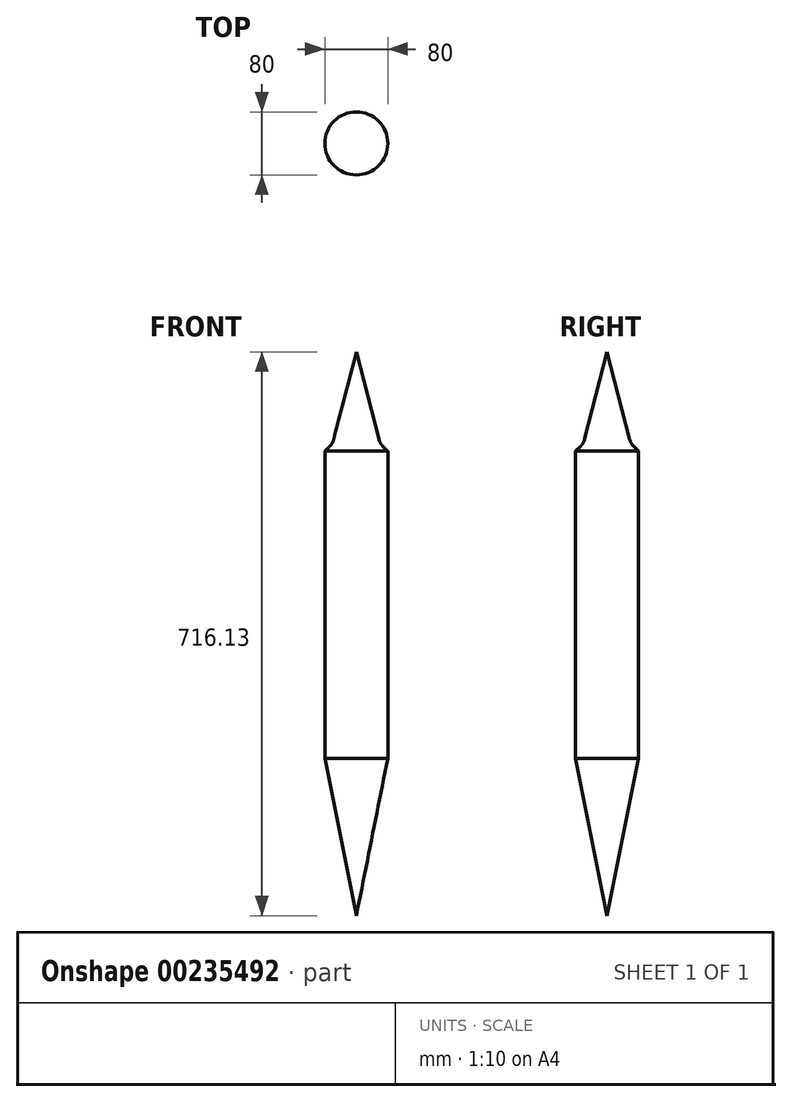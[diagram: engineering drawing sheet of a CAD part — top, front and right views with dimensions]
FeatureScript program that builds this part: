
annotation { "Feature Type Name" : "Feature", "Feature Type Description" : "" }
export const myFeature = defineFeature(function(context is Context, id is Id, definition is map)
    precondition{}
    {
        {
            var Q0;
            Q0=qCreatedBy(makeId("Top.planeOp"),FACE);
            var sketch = newSketch(context, id + "F0", { "sketchPlane" : qUnion([Q0])});
            skCircle(sketch, "E0", {"center": v(0, 0) * mm, "radius": 40 * mm});
            skSolve(sketch);
        }
        {
            var Q0;
            Q0=makeQuery(id+"F0.imprint","IMPRINT",FACE,{"disambiguationData":[TD([[makeQuery(id+"F0.imprint","IMPRINT",EDGE,{"derivedFrom":sQuery(id+"F0.wireOp",EDGE,"E0")}),1.0]])]});
            extrude(context, id + "F1", {"entities" : qUnion([Q0]), "oppositeDirection" : true, "depth" : 400 * mm});
        }
        {
            var Q0;
            Q0=qCreatedBy(makeId("Front.planeOp"),FACE);
            var sketch = newSketch(context, id + "F2", { "sketchPlane" : qUnion([Q0])});
            skLineSegment(sketch, "E1", {"start": v(-40, -10) * mm, "end": v(-40, 0) * mm});
            skPoint(sketch, "E2", {"position": v(-30, 0) * mm});
            skLineSegment(sketch, "E3", {"start": v(-30, 0) * mm, "end": v(-40, -10) * mm});
            skLineSegment(sketch, "E4", {"start": v(0, 22.48) * mm, "end": v(0, -30.24) * mm, "construction": true});
            skLineSegment(sketch, "E5", {"start": v(-40, 0) * mm, "end": v(-30, 0) * mm});
            skSolve(sketch);
        }
        {
            var Q0;
            Q0=makeQuery(id+"F2.imprint","IMPRINT",FACE,{"disambiguationData":[TD([[makeQuery(id+"F2.imprint","IMPRINT",EDGE,{"derivedFrom":sQuery(id+"F2.wireOp",EDGE,"E1")}),-1.0]])]});
            var Q1;
            Q1=sQuery(id+"F2.wireOp",EDGE,"E4");
            revolve(context, id + "F3", {"operationType" : NewBodyOperationType.REMOVE, "entities" : qUnion([Q0]), "axis" : qUnion([Q1]), "revolveType" : RevolveType.FULL, "oppositeDirection" : true});
        }
        {
            var Q0;
            Q0=qCreatedBy(makeId("Front.planeOp"),FACE);
            var sketch = newSketch(context, id + "F4", { "sketchPlane" : qUnion([Q0])});
            skLineSegment(sketch, "E6", {"start": v(0, 0) * mm, "end": v(0, 116.13) * mm});
            skLineSegment(sketch, "E7", {"start": v(0, 116.13) * mm, "end": v(-30, 0) * mm});
            skLineSegment(sketch, "E8", {"start": v(-30, 0) * mm, "end": v(0, 0) * mm});
            skSolve(sketch);
        }
        {
            var Q0;
            Q0=makeQuery(id+"F4.imprint","IMPRINT",FACE,{"disambiguationData":[TD([[makeQuery(id+"F4.imprint","IMPRINT",EDGE,{"derivedFrom":sQuery(id+"F4.wireOp",EDGE,"E6")}),1.0]])]});
            var Q1;
            Q1=sQuery(id+"F4.wireOp",EDGE,"E6");
            revolve(context, id + "F5", {"operationType" : NewBodyOperationType.ADD, "entities" : qUnion([Q0]), "axis" : qUnion([Q1]), "revolveType" : RevolveType.FULL});
        }
        {
            var Q0;
            Q0=makeQuery(id+"F5.boolean.opBoolean","MERGE",EDGE,{"derivedFrom":[makeQuery(id+"F3.boolean.opBoolean","COPY",EDGE,{"derivedFrom":makeQuery(id+"F3.opRevolve","SWEPT_EDGE",EDGE,{"disambiguationData":[OSD([sQuery(id+"F2.wireOp",EDGE,"E3"),sQuery(id+"F2.wireOp",EDGE,"E5")])]})}),makeQuery(id+"F5.opRevolve","SWEPT_EDGE",EDGE,{"disambiguationData":[OSD([sQuery(id+"F4.wireOp",EDGE,"E7"),sQuery(id+"F4.wireOp",EDGE,"E8")])]})]});
            fillet(context, id + "F6", {"entities" : qUnion([Q0]), "radius" : 20 * mm, "tangentPropagation" : true, "allowEdgeOverflow" : false});
        }
        {
            var Q0;
            Q0=qCreatedBy(makeId("Front.planeOp"),FACE);
            var sketch = newSketch(context, id + "F7", { "sketchPlane" : qUnion([Q0])});
            skLineSegment(sketch, "E9.0", {"start": v(-40, -400) * mm, "end": v(0, -400) * mm});
            skLineSegment(sketch, "E10", {"start": v(0, -400) * mm, "end": v(0, -600) * mm});
            skPoint(sketch, "E10.endSnap0", {"position": v(0, -400) * mm});
            skLineSegment(sketch, "E11", {"start": v(0, -600) * mm, "end": v(-40, -400) * mm});
            skPoint(sketch, "E12.orphan", {"position": v(0, -357.52) * mm});
            skPoint(sketch, "E13.start.orphan", {"position": v(40, -400) * mm});
            skSolve(sketch);
        }
        {
            var Q0;
            Q0=makeQuery(id+"F7.imprint","IMPRINT",FACE,{"disambiguationData":[TD([[makeQuery(id+"F7.imprint","IMPRINT",EDGE,{"derivedFrom":sQuery(id+"F7.wireOp",EDGE,"E9.0")}),-1.0]])]});
            var Q1;
            Q1=sQuery(id+"F7.wireOp",EDGE,"E10");
            revolve(context, id + "F8", {"operationType" : NewBodyOperationType.ADD, "entities" : qUnion([Q0]), "axis" : qUnion([Q1]), "revolveType" : RevolveType.FULL});
        }
    });
